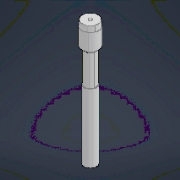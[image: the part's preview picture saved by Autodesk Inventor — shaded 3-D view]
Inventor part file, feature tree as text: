
AUTODESK INVENTOR PART (.ipt)
format: ipt  version: 2025.3 (Build 293356000, 356)  size: 167,424 bytes
history: native  units: mm
features: sketch x2, revolve x1, extrude x1, projected_geometry x1
ambient origin geometry x8: Origin, YZ Plane, XZ Plane, XY Plane, X Axis, Y Axis, Z Axis, Center Point
bodies: Solid1 (feature_tree)
feature tree (5):
  revolve  "Revolution1"  [1 undecoded]
  extrude  "Extrusion1"  Depth=4.0mm
  sketch  "Sketch1"  dims[d1=45.0deg d2=0.872665mm]
  sketch  "Sketch2"  dims[d6=1.2mm d7=4.0mm d9=8.0mm d10=90.0deg d11=45.0deg d12=7.1mm d13=10.0mm d14=0.0mm]
  projected_geometry  "Projected Loop1"
note: 1 required parameter value undecoded (feature->parameter linkage not recoverable at this tier; creation-order binding heuristic only, values carry confidence <= 0.55)
